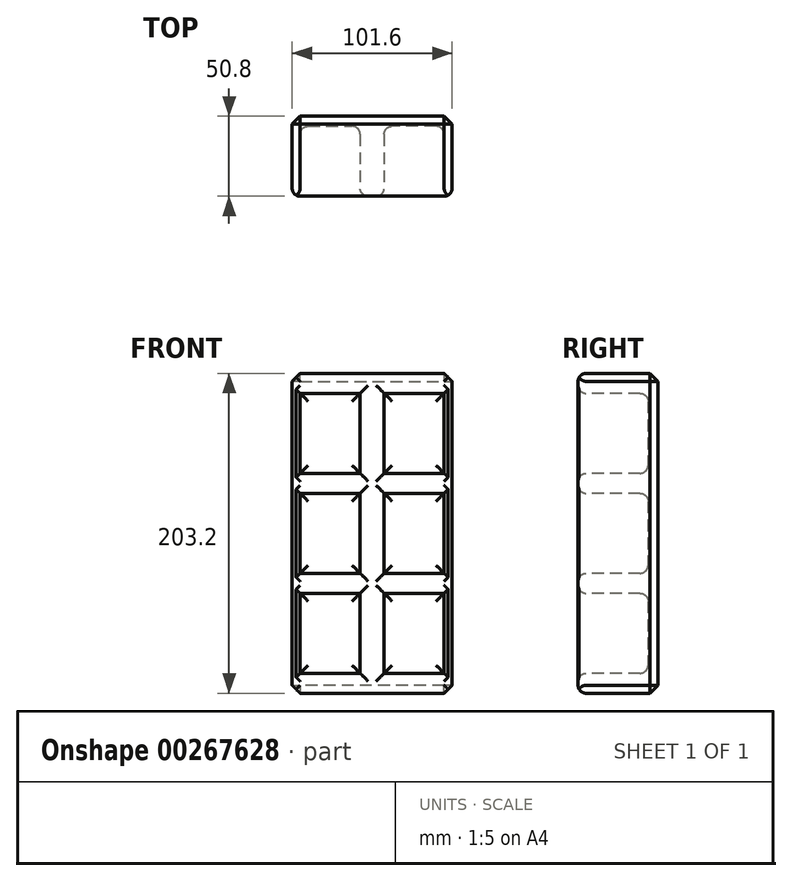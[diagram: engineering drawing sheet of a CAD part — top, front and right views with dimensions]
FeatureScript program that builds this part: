
annotation { "Feature Type Name" : "Feature", "Feature Type Description" : "" }
export const myFeature = defineFeature(function(context is Context, id is Id, definition is map)
    precondition{}
    {
        {
            var Q0;
            Q0=qCreatedBy(makeId("Front.planeOp"),FACE);
            var sketch = newSketch(context, id + "F0", { "sketchPlane" : qUnion([Q0])});
            skLineSegment(sketch, "E0.bottom", {"start": v(50.8, -101.6) * mm, "end": v(-50.8, -101.6) * mm});
            skLineSegment(sketch, "E0.top", {"start": v(50.8, 101.6) * mm, "end": v(-50.8, 101.6) * mm});
            skLineSegment(sketch, "E0.left", {"start": v(50.8, -101.6) * mm, "end": v(50.8, 101.6) * mm});
            skLineSegment(sketch, "E0.right", {"start": v(-50.8, -101.6) * mm, "end": v(-50.8, 101.6) * mm});
            skPoint(sketch, "E0.middle", {"position": v(0, 0) * mm});
            skSolve(sketch);
        }
        {
            var Q0;
            Q0 = qSketchRegion(id + "F0", true);
            extrude(context, id + "F1", {"entities" : qUnion([Q0]), "endBound" : BoundingType.SYMMETRIC, "depth" : 50.8 * mm});
        }
        {
            var Q0;
            Q0=makeQuery(id+"F1.opExtrude","CAP_FACE",FACE,{"disambiguationData":[OSD([sQuery(id+"F0.wireOp",EDGE,"E0.bottom"),sQuery(id+"F0.wireOp",EDGE,"E0.top"),sQuery(id+"F0.wireOp",EDGE,"E0.left"),sQuery(id+"F0.wireOp",EDGE,"E0.right")])],"isStart":false});
            var sketch = newSketch(context, id + "F2", { "sketchPlane" : qUnion([Q0])});
            skLineSegment(sketch, "E1", {"start": v(-50.8, 101.6) * mm, "end": v(-50.8, 88.9) * mm});
            skLineSegment(sketch, "E2", {"start": v(50.8, 101.6) * mm, "end": v(50.8, 88.9) * mm});
            skLineSegment(sketch, "E3", {"start": v(-50.8, 38.1) * mm, "end": v(-50.8, 25.4) * mm});
            skLineSegment(sketch, "E4", {"start": v(50.8, 38.1) * mm, "end": v(50.8, 25.4) * mm});
            skLineSegment(sketch, "E5", {"start": v(-50.8, 88.9) * mm, "end": v(-45.72, 88.9) * mm});
            skLineSegment(sketch, "E6", {"start": v(50.8, 88.9) * mm, "end": v(45.72, 88.9) * mm});
            skLineSegment(sketch, "E7.bottom", {"start": v(-45.72, 88.9) * mm, "end": v(-7.62, 88.9) * mm});
            skLineSegment(sketch, "E7.top", {"start": v(-45.72, 38.1) * mm, "end": v(-7.62, 38.1) * mm});
            skLineSegment(sketch, "E7.left", {"start": v(-45.72, 88.9) * mm, "end": v(-45.72, 38.1) * mm});
            skLineSegment(sketch, "E7.right", {"start": v(-7.62, 88.9) * mm, "end": v(-7.62, 38.1) * mm});
            skLineSegment(sketch, "E8.bottom", {"start": v(45.72, 88.9) * mm, "end": v(7.62, 88.9) * mm});
            skLineSegment(sketch, "E8.top", {"start": v(45.72, 38.1) * mm, "end": v(7.62, 38.1) * mm});
            skLineSegment(sketch, "E8.left", {"start": v(45.72, 88.9) * mm, "end": v(45.72, 38.1) * mm});
            skLineSegment(sketch, "E8.right", {"start": v(7.62, 88.9) * mm, "end": v(7.62, 38.1) * mm});
            skLineSegment(sketch, "E9", {"start": v(-50.8, 25.4) * mm, "end": v(-45.72, 25.4) * mm});
            skLineSegment(sketch, "E10", {"start": v(50.8, 25.4) * mm, "end": v(45.72, 25.4) * mm});
            skLineSegment(sketch, "E11.bottom", {"start": v(-45.72, 25.4) * mm, "end": v(-7.62, 25.4) * mm});
            skLineSegment(sketch, "E11.top", {"start": v(-45.72, -25.4) * mm, "end": v(-7.62, -25.4) * mm});
            skLineSegment(sketch, "E11.left", {"start": v(-45.72, 25.4) * mm, "end": v(-45.72, -25.4) * mm});
            skLineSegment(sketch, "E11.right", {"start": v(-7.62, 25.4) * mm, "end": v(-7.62, -25.4) * mm});
            skLineSegment(sketch, "E12.bottom", {"start": v(45.72, 25.4) * mm, "end": v(7.62, 25.4) * mm});
            skLineSegment(sketch, "E12.top", {"start": v(45.72, -25.4) * mm, "end": v(7.62, -25.4) * mm});
            skLineSegment(sketch, "E12.left", {"start": v(45.72, 25.4) * mm, "end": v(45.72, -25.4) * mm});
            skLineSegment(sketch, "E12.right", {"start": v(7.62, 25.4) * mm, "end": v(7.62, -25.4) * mm});
            skLineSegment(sketch, "E13", {"start": v(-50.8, -25.4) * mm, "end": v(-50.8, -38.1) * mm});
            skLineSegment(sketch, "E14", {"start": v(50.8, -25.4) * mm, "end": v(50.8, -38.1) * mm});
            skLineSegment(sketch, "E15", {"start": v(-50.8, -38.1) * mm, "end": v(-45.72, -38.1) * mm});
            skLineSegment(sketch, "E16", {"start": v(50.8, -38.1) * mm, "end": v(45.72, -38.1) * mm});
            skLineSegment(sketch, "E17.bottom", {"start": v(-45.72, -38.1) * mm, "end": v(-7.62, -38.1) * mm});
            skLineSegment(sketch, "E17.top", {"start": v(-45.72, -88.9) * mm, "end": v(-7.62, -88.9) * mm});
            skLineSegment(sketch, "E17.left", {"start": v(-45.72, -38.1) * mm, "end": v(-45.72, -88.9) * mm});
            skLineSegment(sketch, "E17.right", {"start": v(-7.62, -38.1) * mm, "end": v(-7.62, -88.9) * mm});
            skLineSegment(sketch, "E18.bottom", {"start": v(45.72, -38.1) * mm, "end": v(7.62, -38.1) * mm});
            skLineSegment(sketch, "E18.top", {"start": v(45.72, -88.9) * mm, "end": v(7.62, -88.9) * mm});
            skLineSegment(sketch, "E18.left", {"start": v(45.72, -38.1) * mm, "end": v(45.72, -88.9) * mm});
            skLineSegment(sketch, "E18.right", {"start": v(7.62, -38.1) * mm, "end": v(7.62, -88.9) * mm});
            skSolve(sketch);
        }
        {
            var Q0;
            Q0=makeQuery(id+"F2.imprint","IMPRINT",FACE,{"disambiguationData":[TD([[makeQuery(id+"F2.imprint","IMPRINT",EDGE,{"derivedFrom":sQuery(id+"F2.wireOp",EDGE,"E7.bottom")}),-1.0]])]});
            var Q1;
            Q1=makeQuery(id+"F2.imprint","IMPRINT",FACE,{"disambiguationData":[TD([[makeQuery(id+"F2.imprint","IMPRINT",EDGE,{"derivedFrom":sQuery(id+"F2.wireOp",EDGE,"E8.bottom")}),1.0]])]});
            var Q2;
            Q2=makeQuery(id+"F2.imprint","IMPRINT",FACE,{"disambiguationData":[TD([[makeQuery(id+"F2.imprint","IMPRINT",EDGE,{"derivedFrom":sQuery(id+"F2.wireOp",EDGE,"E12.bottom")}),1.0]])]});
            var Q3;
            Q3=makeQuery(id+"F2.imprint","IMPRINT",FACE,{"disambiguationData":[TD([[makeQuery(id+"F2.imprint","IMPRINT",EDGE,{"derivedFrom":sQuery(id+"F2.wireOp",EDGE,"E11.bottom")}),-1.0]])]});
            var Q4;
            Q4=makeQuery(id+"F2.imprint","IMPRINT",FACE,{"disambiguationData":[TD([[makeQuery(id+"F2.imprint","IMPRINT",EDGE,{"derivedFrom":sQuery(id+"F2.wireOp",EDGE,"E17.bottom")}),-1.0]])]});
            var Q5;
            Q5=makeQuery(id+"F2.imprint","IMPRINT",FACE,{"disambiguationData":[TD([[makeQuery(id+"F2.imprint","IMPRINT",EDGE,{"derivedFrom":sQuery(id+"F2.wireOp",EDGE,"E18.bottom")}),1.0]])]});
            extrude(context, id + "F3", {"entities" : qUnion([Q0, Q1, Q2, Q3, Q4, Q5]), "operationType" : NewBodyOperationType.REMOVE, "oppositeDirection" : true, "depth" : 44.45 * mm});
        }
        {
            var Q0;
            Q0=makeQuery(id+"F3.boolean.opBoolean","COPY",FACE,{"derivedFrom":makeQuery(id+"F3.opExtrude","CAP_FACE",FACE,{"disambiguationData":[OSD([sQuery(id+"F2.wireOp",EDGE,"E7.bottom"),sQuery(id+"F2.wireOp",EDGE,"E7.top"),sQuery(id+"F2.wireOp",EDGE,"E7.left"),sQuery(id+"F2.wireOp",EDGE,"E7.right")])],"isStart":false})});
            var Q1;
            Q1=makeQuery(id+"F3.boolean.opBoolean","COPY",FACE,{"derivedFrom":makeQuery(id+"F3.opExtrude","CAP_FACE",FACE,{"disambiguationData":[OSD([sQuery(id+"F2.wireOp",EDGE,"E8.bottom"),sQuery(id+"F2.wireOp",EDGE,"E8.top"),sQuery(id+"F2.wireOp",EDGE,"E8.left"),sQuery(id+"F2.wireOp",EDGE,"E8.right")])],"isStart":false})});
            var Q2;
            Q2=makeQuery(id+"F3.boolean.opBoolean","COPY",FACE,{"derivedFrom":makeQuery(id+"F3.opExtrude","CAP_FACE",FACE,{"disambiguationData":[OSD([sQuery(id+"F2.wireOp",EDGE,"E11.bottom"),sQuery(id+"F2.wireOp",EDGE,"E11.top"),sQuery(id+"F2.wireOp",EDGE,"E11.left"),sQuery(id+"F2.wireOp",EDGE,"E11.right")])],"isStart":false})});
            var Q3;
            Q3=makeQuery(id+"F3.boolean.opBoolean","COPY",FACE,{"derivedFrom":makeQuery(id+"F3.opExtrude","CAP_FACE",FACE,{"disambiguationData":[OSD([sQuery(id+"F2.wireOp",EDGE,"E12.bottom"),sQuery(id+"F2.wireOp",EDGE,"E12.top"),sQuery(id+"F2.wireOp",EDGE,"E12.left"),sQuery(id+"F2.wireOp",EDGE,"E12.right")])],"isStart":false})});
            var Q4;
            Q4=makeQuery(id+"F3.boolean.opBoolean","COPY",FACE,{"derivedFrom":makeQuery(id+"F3.opExtrude","CAP_FACE",FACE,{"disambiguationData":[OSD([sQuery(id+"F2.wireOp",EDGE,"E17.bottom"),sQuery(id+"F2.wireOp",EDGE,"E17.top"),sQuery(id+"F2.wireOp",EDGE,"E17.left"),sQuery(id+"F2.wireOp",EDGE,"E17.right")])],"isStart":false})});
            var Q5;
            Q5=makeQuery(id+"F3.boolean.opBoolean","COPY",FACE,{"derivedFrom":makeQuery(id+"F3.opExtrude","CAP_FACE",FACE,{"disambiguationData":[OSD([sQuery(id+"F2.wireOp",EDGE,"E18.bottom"),sQuery(id+"F2.wireOp",EDGE,"E18.top"),sQuery(id+"F2.wireOp",EDGE,"E18.left"),sQuery(id+"F2.wireOp",EDGE,"E18.right")])],"isStart":false})});
            var Q6;
            Q6=makeQuery(id+"F1.opExtrude","CAP_FACE",FACE,{"disambiguationData":[OSD([sQuery(id+"F0.wireOp",EDGE,"E0.bottom"),sQuery(id+"F0.wireOp",EDGE,"E0.top"),sQuery(id+"F0.wireOp",EDGE,"E0.left"),sQuery(id+"F0.wireOp",EDGE,"E0.right")])],"isStart":false});
            fillet(context, id + "F4", {"entities" : qUnion([Q0, Q1, Q2, Q3, Q4, Q5, Q6]), "radius" : 5.08 * mm, "tangentPropagation" : true, "allowEdgeOverflow" : false});
        }
        {
            var Q0;
            Q0=makeQuery(id+"F1.opExtrude","CAP_FACE",FACE,{"disambiguationData":[OSD([sQuery(id+"F0.wireOp",EDGE,"E0.bottom"),sQuery(id+"F0.wireOp",EDGE,"E0.top"),sQuery(id+"F0.wireOp",EDGE,"E0.left"),sQuery(id+"F0.wireOp",EDGE,"E0.right")])],"isStart":true});
            var Q1;
            Q1=makeQuery(id+"F1.opExtrude","SWEPT_FACE",FACE,{"disambiguationData":[OSD([sQuery(id+"F0.wireOp",EDGE,"E0.left")])]});
            var Q2;
            Q2=makeQuery(id+"F1.opExtrude","SWEPT_FACE",FACE,{"disambiguationData":[OSD([sQuery(id+"F0.wireOp",EDGE,"E0.top")])]});
            var Q3;
            Q3=makeQuery(id+"F1.opExtrude","SWEPT_FACE",FACE,{"disambiguationData":[OSD([sQuery(id+"F0.wireOp",EDGE,"E0.right")])]});
            var Q4;
            Q4=makeQuery(id+"F1.opExtrude","SWEPT_FACE",FACE,{"disambiguationData":[OSD([sQuery(id+"F0.wireOp",EDGE,"E0.bottom")])]});
            chamfer(context, id + "F5", {"entities" : qUnion([Q0, Q1, Q2, Q3, Q4]), "width" : 5.08 * mm, "tangentPropagation" : true});
        }
    });
